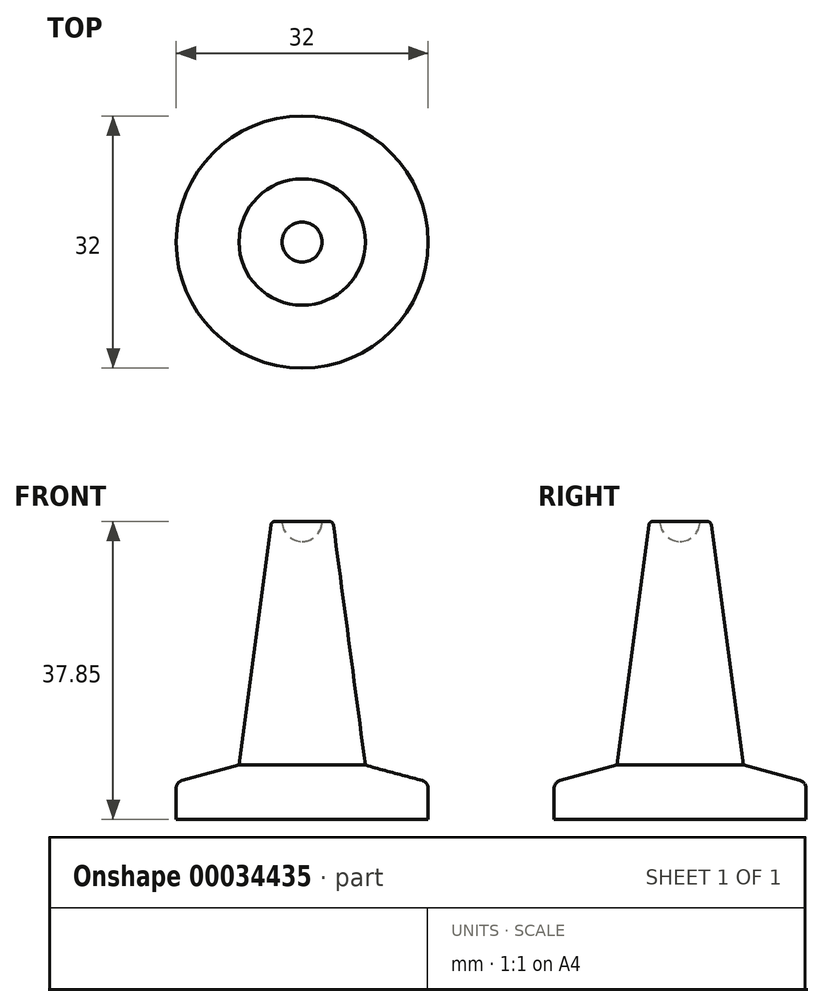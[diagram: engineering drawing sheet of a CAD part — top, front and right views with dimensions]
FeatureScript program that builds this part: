
annotation { "Feature Type Name" : "Feature", "Feature Type Description" : "" }
export const myFeature = defineFeature(function(context is Context, id is Id, definition is map)
    precondition{}
    {
        {
            var Q0;
            Q0=qCreatedBy(makeId("Front.planeOp"),FACE);
            var sketch = newSketch(context, id + "F0", { "sketchPlane" : qUnion([Q0])});
            skLineSegment(sketch, "E0", {"start": v(0, 37.85) * mm, "end": v(0, 0) * mm, "construction": true});
            skLineSegment(sketch, "E1", {"start": v(0, 0) * mm, "end": v(16, 0) * mm});
            skPoint(sketch, "E2", {"position": v(0, 35.3) * mm});
            skLineSegment(sketch, "E3", {"start": v(3.91, 46.45) * mm, "end": v(3.91, 0) * mm, "construction": true});
            skLineSegment(sketch, "E4", {"start": v(8.03, 0) * mm, "end": v(8.03, 19.82) * mm, "construction": true});
            skLineSegment(sketch, "E5", {"start": v(0, 6.9) * mm, "end": v(26.29, 6.9) * mm, "construction": true});
            skPoint(sketch, "E6", {"position": v(8.03, 6.9) * mm});
            skPoint(sketch, "E7", {"position": v(3.91, 37.85) * mm});
            skLineSegment(sketch, "E8", {"start": v(3.91, 37.85) * mm, "end": v(8.03, 6.9) * mm});
            skLineSegment(sketch, "E9", {"start": v(0, 4.72) * mm, "end": v(26.07, 4.72) * mm, "construction": true});
            skLineSegment(sketch, "E10", {"start": v(16, 0) * mm, "end": v(16, 4.72) * mm});
            skLineSegment(sketch, "E11", {"start": v(16, 4.72) * mm, "end": v(8.03, 6.9) * mm});
            skArc(sketch, "E12", {"start": v(0, 35.3) * mm, "mid": v(1.8, 36.05) * mm, "end": v(2.54, 37.85) * mm});
            skLineSegment(sketch, "E13", {"start": v(0, 37.85) * mm, "end": v(3.91, 37.85) * mm, "construction": true});
            skLineSegment(sketch, "E14", {"start": v(2.54, 37.85) * mm, "end": v(3.91, 37.85) * mm});
            skLineSegment(sketch, "E15", {"start": v(0, 35.3) * mm, "end": v(0, 0) * mm});
            skSolve(sketch);
        }
        {
            var Q0;
            Q0=makeQuery(id+"F0.imprint","IMPRINT",FACE,{"disambiguationData":[TD([[makeQuery(id+"F0.imprint","IMPRINT",EDGE,{"derivedFrom":sQuery(id+"F0.wireOp",EDGE,"E1")}),1.0]])]});
            var Q1;
            Q1=sQuery(id+"F0.wireOp",EDGE,"E15");
            revolve(context, id + "F1", {"entities" : qUnion([Q0]), "axis" : qUnion([Q1]), "revolveType" : RevolveType.FULL});
        }
        {
            var Q0;
            Q0=makeQuery(id+"F1.opRevolve","SWEPT_EDGE",EDGE,{"disambiguationData":[OSD([sQuery(id+"F0.wireOp",EDGE,"E10"),sQuery(id+"F0.wireOp",EDGE,"E11")])]});
            fillet(context, id + "F2", {"entities" : qUnion([Q0]), "radius" : 1.02 * mm, "tangentPropagation" : true, "allowEdgeOverflow" : false});
        }
        {
            var Q0;
            Q0=makeQuery(id+"F1.opRevolve","SWEPT_EDGE",EDGE,{"disambiguationData":[OSD([sQuery(id+"F0.wireOp",EDGE,"E8"),sQuery(id+"F0.wireOp",EDGE,"E14")])]});
            fillet(context, id + "F3", {"entities" : qUnion([Q0]), "radius" : 0.5 * mm, "tangentPropagation" : true, "allowEdgeOverflow" : false});
        }
    });
